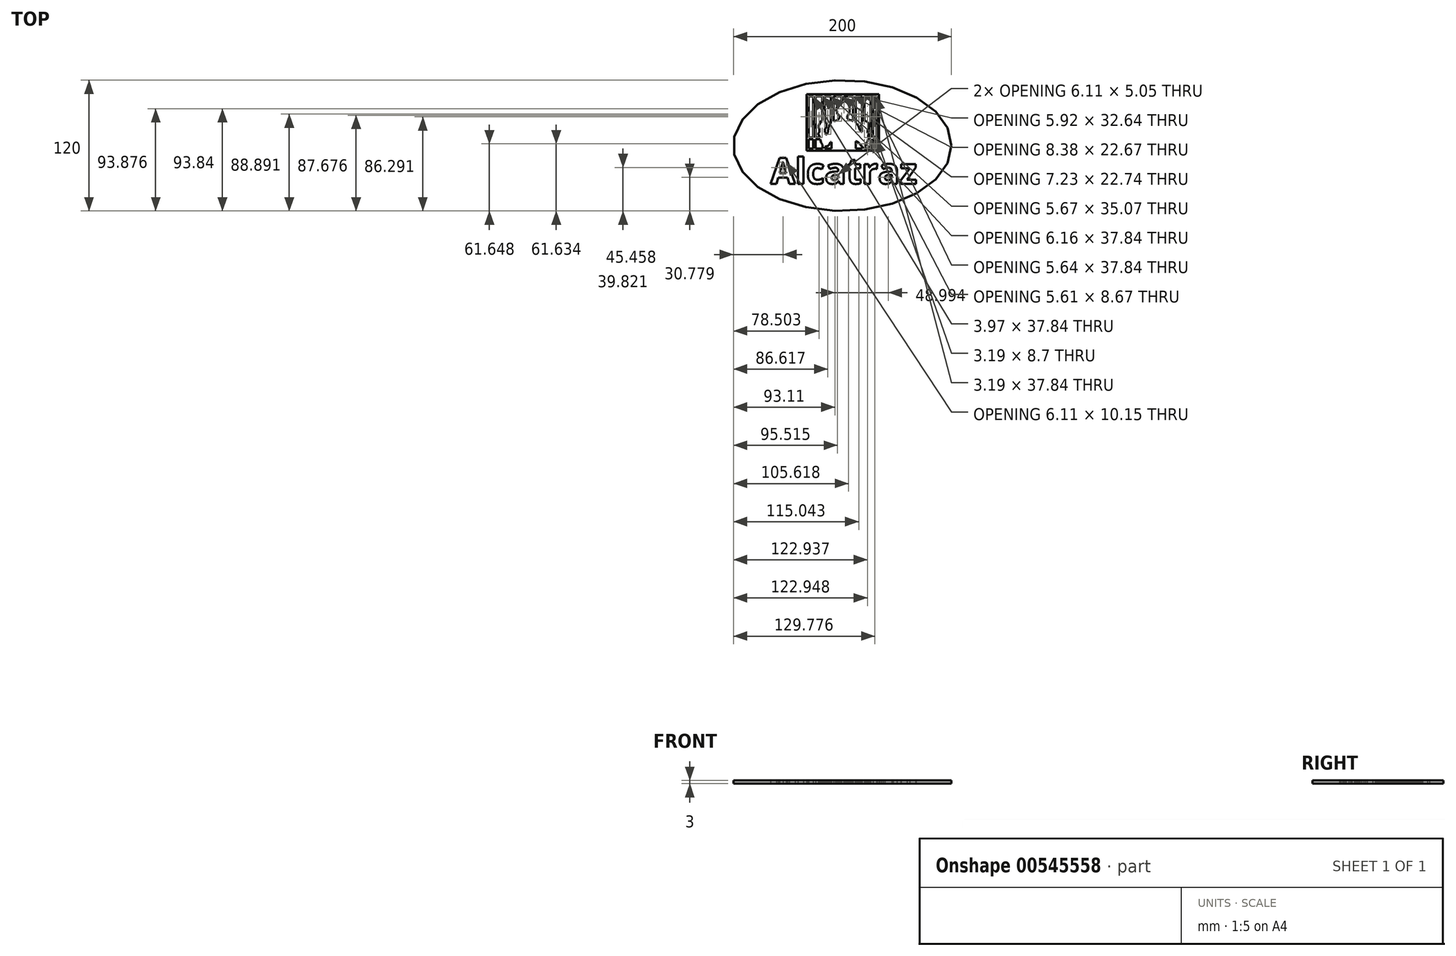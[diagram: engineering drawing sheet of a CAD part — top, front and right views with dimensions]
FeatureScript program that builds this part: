
annotation { "Feature Type Name" : "Feature", "Feature Type Description" : "" }
export const myFeature = defineFeature(function(context is Context, id is Id, definition is map)
    precondition{}
    {
        {
            var Q0;
            Q0=qCreatedBy(makeId("Top.planeOp"),FACE);
            var sketch = newSketch(context, id + "F0", { "sketchPlane" : qUnion([Q0])});
            skEllipse(sketch, "E0", {"center": v(0, 0) * mm, "majorRadius": 100 * mm, "minorRadius": 60 * mm, "majorAxis": v(1, 0)});
            skFitSpline(sketch, "E1.0", {"points": [v(94.93, -2.57) * mm, v(95.04, 0) * mm, v(94.93, 2.57) * mm, v(94.5, 5.97) * mm, v(93.46, 10.19) * mm, v(91.36, 15.2) * mm, v(88.41, 20.14) * mm, v(84.62, 24.96) * mm, v(80.76, 28.83) * mm, v(77.26, 31.82) * mm, v(74.43, 34) * mm, v(71.4, 36.11) * mm, v(68.17, 38.15) * mm, v(64.76, 40.1) * mm, v(61.2, 41.94) * mm, v(57.49, 43.68) * mm, v(52.36, 45.84) * mm, v(45.64, 48.25) * mm, v(37.12, 50.66) * mm, v(28.24, 52.57) * mm, v(20.58, 53.73) * mm, v(14.33, 54.39) * mm, v(9.6, 54.74) * mm, v(5.61, 54.92) * mm, v(2.4, 54.99) * mm, v(0, 55) * mm, v(-2.41, 54.99) * mm, v(-5.61, 54.92) * mm, v(-9.6, 54.74) * mm, v(-14.33, 54.39) * mm, v(-20.58, 53.73) * mm, v(-28.24, 52.57) * mm, v(-37.12, 50.66) * mm, v(-45.64, 48.25) * mm, v(-52.36, 45.84) * mm, v(-57.49, 43.68) * mm, v(-61.2, 41.94) * mm, v(-64.76, 40.1) * mm, v(-68.17, 38.15) * mm, v(-71.4, 36.11) * mm, v(-74.43, 34) * mm, v(-77.26, 31.82) * mm, v(-80.76, 28.83) * mm, v(-84.62, 24.96) * mm, v(-88.41, 20.14) * mm, v(-91.36, 15.2) * mm, v(-93.46, 10.19) * mm, v(-94.5, 5.97) * mm, v(-94.93, 2.57) * mm, v(-95.04, 0) * mm, v(-94.93, -2.57) * mm, v(-94.5, -5.97) * mm, v(-93.46, -10.19) * mm, v(-91.36, -15.2) * mm, v(-88.41, -20.14) * mm, v(-84.62, -24.96) * mm, v(-80.76, -28.83) * mm, v(-77.26, -31.82) * mm, v(-74.43, -34) * mm, v(-71.4, -36.11) * mm, v(-68.17, -38.15) * mm, v(-64.76, -40.1) * mm, v(-61.2, -41.94) * mm, v(-57.49, -43.68) * mm, v(-52.36, -45.84) * mm, v(-45.64, -48.25) * mm, v(-37.12, -50.66) * mm, v(-28.24, -52.57) * mm, v(-20.58, -53.73) * mm, v(-14.33, -54.39) * mm, v(-9.6, -54.74) * mm, v(-5.61, -54.92) * mm, v(-2.41, -54.99) * mm, v(0, -55) * mm, v(2.4, -54.99) * mm, v(5.61, -54.92) * mm, v(9.6, -54.74) * mm, v(14.33, -54.39) * mm, v(20.58, -53.73) * mm, v(28.24, -52.57) * mm, v(37.12, -50.66) * mm, v(45.64, -48.25) * mm, v(52.36, -45.84) * mm, v(57.49, -43.68) * mm, v(61.2, -41.94) * mm, v(64.76, -40.1) * mm, v(68.17, -38.15) * mm, v(71.4, -36.11) * mm, v(74.43, -34) * mm, v(77.26, -31.82) * mm, v(80.76, -28.83) * mm, v(84.62, -24.96) * mm, v(88.41, -20.14) * mm, v(91.36, -15.2) * mm, v(93.46, -10.19) * mm, v(94.5, -5.97) * mm, v(94.93, -2.57) * mm, v(95.04, 0) * mm, v(94.93, 2.57) * mm, v(94.93, -2.57) * mm]});
            skSolve(sketch);
        }
        {
            var Q0;
            Q0=makeQuery(id+"F0.imprint","IMPRINT",FACE,{"disambiguationData":[TD([[makeQuery(id+"F0.imprint","IMPRINT",EDGE,{"derivedFrom":sQuery(id+"F0.wireOp",EDGE,"E0")}),1.0]])]});
            var Q1;
            Q1=sQuery(id+"F0.wireOp",EDGE,"E0");
            var Q2;
            Q2=sQuery(id+"F0.wireOp",EDGE,"E1.0");
            extrude(context, id + "F1", {"entities" : qUnion([Q0]), "surfaceEntities" : qUnion([Q1, Q2]), "depth" : 3 * mm, "offsetDistance" : 25 * mm});
        }
        {
            var Q0;
            Q0=qCreatedBy(makeId("Top.planeOp"),FACE);
            var sketch = newSketch(context, id + "F2", { "sketchPlane" : qUnion([Q0])});
            skLineSegment(sketch, "E2", {"start": v(-10.03, -1.92) * mm, "end": v(-10.03, 2.73) * mm});
            skLineSegment(sketch, "E3", {"start": v(-10.03, 2.73) * mm, "end": v(-10.27, 3.12) * mm});
            skLineSegment(sketch, "E4", {"start": v(-10.27, 3.12) * mm, "end": v(-10.92, 3.12) * mm});
            skLineSegment(sketch, "E5", {"start": v(-10.92, 3.12) * mm, "end": v(-11.14, 2.54) * mm});
            skLineSegment(sketch, "E6", {"start": v(-11.14, 2.54) * mm, "end": v(-12.04, 0.97) * mm});
            skLineSegment(sketch, "E7", {"start": v(-12.04, 0.97) * mm, "end": v(-13.13, -0.16) * mm});
            skLineSegment(sketch, "E8", {"start": v(-13.13, -0.16) * mm, "end": v(-14.02, -0.56) * mm});
            skLineSegment(sketch, "E9", {"start": v(-14.02, -0.56) * mm, "end": v(-15.26, -0.93) * mm});
            skLineSegment(sketch, "E10", {"start": v(-15.26, -0.93) * mm, "end": v(-16.06, -1.25) * mm});
            skLineSegment(sketch, "E11", {"start": v(-16.06, -1.25) * mm, "end": v(-16.06, -2.7) * mm});
            skLineSegment(sketch, "E12", {"start": v(-18.4, -2.7) * mm, "end": v(-18.4, 0.7) * mm});
            skLineSegment(sketch, "E13", {"start": v(-18.4, 0.7) * mm, "end": v(-19.45, 2.73) * mm});
            skLineSegment(sketch, "E14", {"start": v(-19.45, 2.73) * mm, "end": v(-20.03, 4.87) * mm});
            skLineSegment(sketch, "E15", {"start": v(-20.03, 4.87) * mm, "end": v(-20.34, 5.95) * mm});
            skLineSegment(sketch, "E16", {"start": v(-20.9, 7.87) * mm, "end": v(-21.95, 10.53) * mm});
            skLineSegment(sketch, "E17", {"start": v(-21.95, 10.53) * mm, "end": v(-21.95, 11.44) * mm});
            skLineSegment(sketch, "E18", {"start": v(-21.95, 11.44) * mm, "end": v(-21.11, 12.31) * mm});
            skLineSegment(sketch, "E19", {"start": v(-21.11, 12.31) * mm, "end": v(-21.11, 14.95) * mm});
            skLineSegment(sketch, "E20", {"start": v(-21.11, 14.95) * mm, "end": v(-21.47, 15.85) * mm});
            skLineSegment(sketch, "E21", {"start": v(-21.47, 15.85) * mm, "end": v(-21.74, 16.52) * mm});
            skLineSegment(sketch, "E22", {"start": v(-21.74, 16.52) * mm, "end": v(-21.74, 18.05) * mm});
            skLineSegment(sketch, "E23", {"start": v(-21.74, 18.05) * mm, "end": v(-21.02, 19.76) * mm});
            skLineSegment(sketch, "E24", {"start": v(-21.02, 19.76) * mm, "end": v(-20.4, 20.86) * mm});
            skLineSegment(sketch, "E25", {"start": v(-20.4, 20.86) * mm, "end": v(-19.66, 22.15) * mm});
            skLineSegment(sketch, "E26", {"start": v(-19.66, 22.15) * mm, "end": v(-18.79, 23.06) * mm});
            skLineSegment(sketch, "E27", {"start": v(-18.79, 23.06) * mm, "end": v(-18.42, 23.71) * mm});
            skLineSegment(sketch, "E28", {"start": v(-16.02, 21.41) * mm, "end": v(-14.77, 20.7) * mm});
            skLineSegment(sketch, "E29", {"start": v(-14.77, 20.7) * mm, "end": v(-14.55, 19.32) * mm});
            skLineSegment(sketch, "E30", {"start": v(-14.55, 19.32) * mm, "end": v(-14.55, 18.27) * mm});
            skLineSegment(sketch, "E31", {"start": v(-14.55, 18.27) * mm, "end": v(-14.55, 17.44) * mm});
            skLineSegment(sketch, "E32", {"start": v(-14.55, 17.44) * mm, "end": v(-14.55, 16.77) * mm});
            skLineSegment(sketch, "E33", {"start": v(-14.55, 16.77) * mm, "end": v(-15.6, 15.69) * mm});
            skLineSegment(sketch, "E34", {"start": v(-15.6, 15.69) * mm, "end": v(-16.07, 14.86) * mm});
            skLineSegment(sketch, "E35", {"start": v(-16.07, 14.86) * mm, "end": v(-16.07, 12.9) * mm});
            skLineSegment(sketch, "E36", {"start": v(-16.07, 12.9) * mm, "end": v(-15.7, 11.97) * mm});
            skLineSegment(sketch, "E37", {"start": v(-15.7, 11.97) * mm, "end": v(-15.26, 10.85) * mm});
            skLineSegment(sketch, "E38", {"start": v(-15.26, 10.85) * mm, "end": v(-15.26, 10.14) * mm});
            skLineSegment(sketch, "E39", {"start": v(-15.26, 10.14) * mm, "end": v(-14.5, 10.14) * mm});
            skLineSegment(sketch, "E40", {"start": v(-14.5, 10.14) * mm, "end": v(-13.85, 11.27) * mm});
            skLineSegment(sketch, "E41", {"start": v(-13.85, 11.27) * mm, "end": v(-13.27, 12.3) * mm});
            skLineSegment(sketch, "E42", {"start": v(-13.27, 12.3) * mm, "end": v(-13.13, 13.73) * mm});
            skLineSegment(sketch, "E43", {"start": v(-13.13, 13.73) * mm, "end": v(-12.8, 15.35) * mm});
            skLineSegment(sketch, "E44", {"start": v(-12.8, 15.35) * mm, "end": v(-12.46, 17.15) * mm});
            skLineSegment(sketch, "E45", {"start": v(-12.46, 17.15) * mm, "end": v(-11.9, 18.58) * mm});
            skLineSegment(sketch, "E46", {"start": v(-11.9, 18.58) * mm, "end": v(-11.2, 19.79) * mm});
            skLineSegment(sketch, "E47", {"start": v(-11.2, 19.79) * mm, "end": v(-10.55, 20.93) * mm});
            skLineSegment(sketch, "E48", {"start": v(-10.55, 20.93) * mm, "end": v(-10.55, 20.93) * mm});
            skLineSegment(sketch, "E49", {"start": v(-8.1, 22.47) * mm, "end": v(-6.35, 22.74) * mm});
            skLineSegment(sketch, "E50", {"start": v(-6.35, 22.74) * mm, "end": v(-4.99, 23.28) * mm});
            skLineSegment(sketch, "E51", {"start": v(-4.99, 23.28) * mm, "end": v(-3.74, 24.22) * mm});
            skLineSegment(sketch, "E52", {"start": v(-3.74, 24.22) * mm, "end": v(-2.88, 25.11) * mm});
            skLineSegment(sketch, "E53", {"start": v(-2.88, 25.11) * mm, "end": v(-2.3, 26.15) * mm});
            skLineSegment(sketch, "E54", {"start": v(-2.3, 26.15) * mm, "end": v(-2.5, 26.7) * mm});
            skLineSegment(sketch, "E55", {"start": v(-2.5, 26.7) * mm, "end": v(-3.29, 27.44) * mm});
            skLineSegment(sketch, "E56", {"start": v(-3.29, 27.44) * mm, "end": v(-4.06, 28.18) * mm});
            skLineSegment(sketch, "E57", {"start": v(-4.06, 28.18) * mm, "end": v(-4.55, 29.11) * mm});
            skLineSegment(sketch, "E58", {"start": v(-4.55, 29.11) * mm, "end": v(-4.92, 30.06) * mm});
            skLineSegment(sketch, "E59", {"start": v(-4.92, 30.06) * mm, "end": v(-4.92, 31.2) * mm});
            skLineSegment(sketch, "E60", {"start": v(-4.92, 31.2) * mm, "end": v(-5.13, 32.19) * mm});
            skLineSegment(sketch, "E61", {"start": v(-5.13, 32.19) * mm, "end": v(-5.13, 33.32) * mm});
            skLineSegment(sketch, "E62", {"start": v(-5.13, 33.32) * mm, "end": v(-5.13, 34.72) * mm});
            skLineSegment(sketch, "E63", {"start": v(-5.13, 34.72) * mm, "end": v(-4.99, 35.74) * mm});
            skLineSegment(sketch, "E64", {"start": v(-4.99, 35.74) * mm, "end": v(-4.57, 36.85) * mm});
            skLineSegment(sketch, "E65", {"start": v(-4.57, 36.85) * mm, "end": v(-3.92, 37.99) * mm});
            skLineSegment(sketch, "E66", {"start": v(-3.92, 37.99) * mm, "end": v(-3.16, 39.05) * mm});
            skLineSegment(sketch, "E67", {"start": v(-3.16, 39.05) * mm, "end": v(-2.07, 40.2) * mm});
            skLineSegment(sketch, "E68", {"start": v(-2.07, 40.2) * mm, "end": v(-0.87, 40.91) * mm});
            skLineSegment(sketch, "E69", {"start": v(1.43, 40.91) * mm, "end": v(2.56, 40.48) * mm});
            skLineSegment(sketch, "E70", {"start": v(2.56, 40.48) * mm, "end": v(3.54, 39.92) * mm});
            skLineSegment(sketch, "E71", {"start": v(3.54, 39.92) * mm, "end": v(4.3, 39.2) * mm});
            skLineSegment(sketch, "E72", {"start": v(4.3, 39.2) * mm, "end": v(5.12, 38.11) * mm});
            skLineSegment(sketch, "E73", {"start": v(5.12, 38.11) * mm, "end": v(5.78, 36.9) * mm});
            skLineSegment(sketch, "E74", {"start": v(5.78, 36.9) * mm, "end": v(6.25, 35.7) * mm});
            skLineSegment(sketch, "E75", {"start": v(6.25, 35.7) * mm, "end": v(6.54, 34.56) * mm});
            skLineSegment(sketch, "E76", {"start": v(6.54, 34.56) * mm, "end": v(6.62, 33.24) * mm});
            skLineSegment(sketch, "E77", {"start": v(6.62, 33.24) * mm, "end": v(6.62, 31.45) * mm});
            skLineSegment(sketch, "E78", {"start": v(6.62, 31.45) * mm, "end": v(6.44, 30.1) * mm});
            skLineSegment(sketch, "E79", {"start": v(6.44, 30.1) * mm, "end": v(5.72, 28.86) * mm});
            skLineSegment(sketch, "E80", {"start": v(5.72, 28.86) * mm, "end": v(5.05, 27.68) * mm});
            skLineSegment(sketch, "E81", {"start": v(5.05, 27.68) * mm, "end": v(4.71, 26.8) * mm});
            skLineSegment(sketch, "E82", {"start": v(4.71, 26.8) * mm, "end": v(4.43, 26.04) * mm});
            skLineSegment(sketch, "E83", {"start": v(4.43, 26.04) * mm, "end": v(4.48, 25.26) * mm});
            skLineSegment(sketch, "E84", {"start": v(4.48, 25.26) * mm, "end": v(4.76, 24.55) * mm});
            skLineSegment(sketch, "E85", {"start": v(4.76, 24.55) * mm, "end": v(5.54, 24.1) * mm});
            skLineSegment(sketch, "E86", {"start": v(5.54, 24.1) * mm, "end": v(6.25, 23.56) * mm});
            skLineSegment(sketch, "E87", {"start": v(6.25, 23.56) * mm, "end": v(7.38, 23.28) * mm});
            skLineSegment(sketch, "E88", {"start": v(7.38, 23.28) * mm, "end": v(8.42, 23) * mm});
            skLineSegment(sketch, "E89", {"start": v(8.42, 23) * mm, "end": v(9.28, 22.68) * mm});
            skLineSegment(sketch, "E90", {"start": v(9.28, 22.68) * mm, "end": v(9.81, 22.54) * mm});
            skLineSegment(sketch, "E91", {"start": v(12.08, 20.89) * mm, "end": v(13.03, 19.98) * mm});
            skLineSegment(sketch, "E92", {"start": v(13.03, 19.98) * mm, "end": v(13.9, 19.26) * mm});
            skLineSegment(sketch, "E93", {"start": v(13.9, 19.26) * mm, "end": v(14.45, 18.55) * mm});
            skLineSegment(sketch, "E94", {"start": v(14.45, 18.55) * mm, "end": v(14.7, 17.9) * mm});
            skLineSegment(sketch, "E95", {"start": v(14.7, 17.9) * mm, "end": v(14.92, 17.34) * mm});
            skLineSegment(sketch, "E96", {"start": v(14.92, 17.34) * mm, "end": v(15.2, 16.65) * mm});
            skLineSegment(sketch, "E97", {"start": v(15.2, 16.65) * mm, "end": v(15.5, 15.9) * mm});
            skLineSegment(sketch, "E98", {"start": v(15.5, 15.9) * mm, "end": v(15.78, 15.17) * mm});
            skLineSegment(sketch, "E99", {"start": v(15.78, 15.17) * mm, "end": v(16.04, 14.51) * mm});
            skLineSegment(sketch, "E100", {"start": v(16.04, 14.51) * mm, "end": v(16.09, 13.77) * mm});
            skLineSegment(sketch, "E101", {"start": v(16.09, 13.77) * mm, "end": v(16.75, 13.29) * mm});
            skLineSegment(sketch, "E102", {"start": v(16.75, 13.29) * mm, "end": v(17.25, 12.81) * mm});
            skLineSegment(sketch, "E103", {"start": v(17.25, 12.81) * mm, "end": v(17.67, 12.57) * mm});
            skLineSegment(sketch, "E104", {"start": v(17.67, 12.57) * mm, "end": v(18, 12.57) * mm});
            skLineSegment(sketch, "E105", {"start": v(18, 12.57) * mm, "end": v(18, 16.92) * mm});
            skLineSegment(sketch, "E106", {"start": v(18, 16.92) * mm, "end": v(17.53, 17.38) * mm});
            skLineSegment(sketch, "E107", {"start": v(17.53, 17.38) * mm, "end": v(17.14, 17.9) * mm});
            skLineSegment(sketch, "E108", {"start": v(17.14, 17.9) * mm, "end": v(16.9, 18.2) * mm});
            skLineSegment(sketch, "E109", {"start": v(16.9, 18.2) * mm, "end": v(16.87, 18.78) * mm});
            skLineSegment(sketch, "E110", {"start": v(16.87, 18.78) * mm, "end": v(17.5, 19.44) * mm});
            skLineSegment(sketch, "E111", {"start": v(17.5, 19.44) * mm, "end": v(17.9, 19.85) * mm});
            skLineSegment(sketch, "E112", {"start": v(17.9, 19.85) * mm, "end": v(17.9, 45.21) * mm});
            skLineSegment(sketch, "E113", {"start": v(20.12, 45.21) * mm, "end": v(20.12, 22.29) * mm});
            skLineSegment(sketch, "E114", {"start": v(20.12, 22.29) * mm, "end": v(21, 22.63) * mm});
            skLineSegment(sketch, "E115", {"start": v(21, 22.63) * mm, "end": v(21.51, 22.56) * mm});
            skLineSegment(sketch, "E116", {"start": v(21.51, 22.56) * mm, "end": v(22.25, 22.14) * mm});
            skLineSegment(sketch, "E117", {"start": v(22.25, 22.14) * mm, "end": v(23.2, 20.89) * mm});
            skLineSegment(sketch, "E118", {"start": v(23.2, 20.89) * mm, "end": v(24, 20.43) * mm});
            skLineSegment(sketch, "E119", {"start": v(24, 20.43) * mm, "end": v(24.46, 19.26) * mm});
            skLineSegment(sketch, "E120", {"start": v(24.46, 19.26) * mm, "end": v(24.46, 17.38) * mm});
            skLineSegment(sketch, "E121", {"start": v(24.46, 17.38) * mm, "end": v(24.55, 15.9) * mm});
            skLineSegment(sketch, "E122", {"start": v(24.55, 15.9) * mm, "end": v(23.62, 14.94) * mm});
            skLineSegment(sketch, "E123", {"start": v(23.62, 14.94) * mm, "end": v(23.03, 13.9) * mm});
            skLineSegment(sketch, "E124", {"start": v(23.03, 13.9) * mm, "end": v(22.94, 13.67) * mm});
            skLineSegment(sketch, "E125", {"start": v(22.94, 13.67) * mm, "end": v(23.07, 11.57) * mm});
            skLineSegment(sketch, "E126", {"start": v(23.07, 11.57) * mm, "end": v(23.48, 11.47) * mm});
            skLineSegment(sketch, "E127", {"start": v(23.48, 11.47) * mm, "end": v(23.98, 11.28) * mm});
            skLineSegment(sketch, "E128", {"start": v(23.98, 11.28) * mm, "end": v(24.18, 11.17) * mm});
            skLineSegment(sketch, "E129", {"start": v(24.18, 11.17) * mm, "end": v(23.97, 10.7) * mm});
            skLineSegment(sketch, "E130", {"start": v(23.97, 10.7) * mm, "end": v(23.84, 10) * mm});
            skLineSegment(sketch, "E131", {"start": v(23.84, 10) * mm, "end": v(23.7, 8.92) * mm});
            skLineSegment(sketch, "E132", {"start": v(23.7, 8.92) * mm, "end": v(23.7, 8) * mm});
            skLineSegment(sketch, "E133", {"start": v(23.7, 8) * mm, "end": v(23.57, 7.37) * mm});
            skLineSegment(sketch, "E134", {"start": v(23.28, 5.95) * mm, "end": v(23.05, 4.73) * mm});
            skLineSegment(sketch, "E135", {"start": v(23.05, 4.73) * mm, "end": v(22.9, 4) * mm});
            skLineSegment(sketch, "E136", {"start": v(22.9, 4) * mm, "end": v(22.62, 3.23) * mm});
            skLineSegment(sketch, "E137", {"start": v(22.62, 3.23) * mm, "end": v(22.1, 1.87) * mm});
            skLineSegment(sketch, "E138", {"start": v(22.1, 1.87) * mm, "end": v(21.69, 0.78) * mm});
            skLineSegment(sketch, "E139", {"start": v(21.69, 0.78) * mm, "end": v(21.25, -0.38) * mm});
            skLineSegment(sketch, "E140", {"start": v(21.25, -0.38) * mm, "end": v(20.94, -0.93) * mm});
            skLineSegment(sketch, "E141", {"start": v(20.94, -0.93) * mm, "end": v(20.73, -1.29) * mm});
            skLineSegment(sketch, "E142", {"start": v(20.73, -1.29) * mm, "end": v(20.14, -1.29) * mm});
            skLineSegment(sketch, "E143", {"start": v(18.02, -0.27) * mm, "end": v(17.13, 0.24) * mm});
            skLineSegment(sketch, "E144", {"start": v(17.13, 0.24) * mm, "end": v(16.33, 1.03) * mm});
            skLineSegment(sketch, "E145", {"start": v(16.33, 1.03) * mm, "end": v(15.5, 1.83) * mm});
            skLineSegment(sketch, "E146", {"start": v(15.5, 1.83) * mm, "end": v(14.76, 2.53) * mm});
            skLineSegment(sketch, "E147", {"start": v(14.76, 2.53) * mm, "end": v(13.9, 3.15) * mm});
            skLineSegment(sketch, "E148", {"start": v(13.9, 3.15) * mm, "end": v(13.13, 3.72) * mm});
            skLineSegment(sketch, "E149", {"start": v(13.13, 3.72) * mm, "end": v(12.58, 4.03) * mm});
            skLineSegment(sketch, "E150", {"start": v(12.58, 4.03) * mm, "end": v(12.3, 3.92) * mm});
            skLineSegment(sketch, "E151", {"start": v(12.3, 3.92) * mm, "end": v(12.3, 3.02) * mm});
            skLineSegment(sketch, "E152", {"start": v(12.3, 3.02) * mm, "end": v(12.37, 1.88) * mm});
            skLineSegment(sketch, "E153", {"start": v(12.37, 1.88) * mm, "end": v(12.37, 0.66) * mm});
            skLineSegment(sketch, "E154", {"start": v(12.37, 0.66) * mm, "end": v(12.37, -1.92) * mm});
            skLineSegment(sketch, "E155", {"start": v(25.76, 45.21) * mm, "end": v(25.76, 7.37) * mm});
            skLineSegment(sketch, "E156", {"start": v(28.18, -2.7) * mm, "end": v(28.18, 5.98) * mm});
            skLineSegment(sketch, "E157", {"start": v(12.08, 45.21) * mm, "end": v(12.08, 20.89) * mm});
            skLineSegment(sketch, "E158", {"start": v(9.81, 45.21) * mm, "end": v(9.81, 22.54) * mm});
            skLineSegment(sketch, "E159", {"start": v(12.37, -1.92) * mm, "end": v(12.37, -2.7) * mm});
            skLineSegment(sketch, "E160", {"start": v(-10.03, -2.7) * mm, "end": v(-10.03, -1.92) * mm});
            skLineSegment(sketch, "E161", {"start": v(18.02, -0.27) * mm, "end": v(18.02, -2.7) * mm});
            skLineSegment(sketch, "E162", {"start": v(20.14, -2.7) * mm, "end": v(20.14, -1.29) * mm});
            skLineSegment(sketch, "E163", {"start": v(31.37, 6) * mm, "end": v(28.18, 5.98) * mm});
            skLineSegment(sketch, "E164", {"start": v(31.36, 7.37) * mm, "end": v(28.18, 7.37) * mm});
            skLineSegment(sketch, "E165.trimOffspring", {"start": v(25.76, 5.97) * mm, "end": v(25.76, -2.7) * mm});
            skLineSegment(sketch, "E166.trimOffspring", {"start": v(28.18, 7.37) * mm, "end": v(28.18, 45.21) * mm});
            skLineSegment(sketch, "E167.trimOffspring", {"start": v(25.76, 5.97) * mm, "end": v(23.28, 5.95) * mm});
            skLineSegment(sketch, "E168.trimOffspring", {"start": v(25.76, 7.37) * mm, "end": v(23.57, 7.37) * mm});
            skLineSegment(sketch, "E169", {"start": v(-24.58, -2.7) * mm, "end": v(-24.58, 5.95) * mm});
            skLineSegment(sketch, "E170", {"start": v(-26.85, 45.21) * mm, "end": v(-26.85, 7.37) * mm});
            skLineSegment(sketch, "E171", {"start": v(23.28, 5.95) * mm, "end": v(-24.58, 5.95) * mm});
            skLineSegment(sketch, "E172", {"start": v(23.57, 7.37) * mm, "end": v(-24.58, 7.37) * mm});
            skPoint(sketch, "E172.endSnap0", {"position": v(24.66, 7.37) * mm});
            skLineSegment(sketch, "E173.trimOffspring", {"start": v(-26.85, 5.95) * mm, "end": v(-26.85, -2.7) * mm});
            skLineSegment(sketch, "E174.trimOffspring", {"start": v(-24.58, 7.37) * mm, "end": v(-24.58, 45.21) * mm});
            skLineSegment(sketch, "E175.trimOffspring", {"start": v(-26.85, 7.37) * mm, "end": v(-30.82, 7.37) * mm});
            skLineSegment(sketch, "E176.trimOffspring", {"start": v(-26.85, 5.95) * mm, "end": v(-30.82, 5.95) * mm});
            skLineSegment(sketch, "E177.trimOffspring", {"start": v(-20.75, 7.37) * mm, "end": v(-20.9, 7.87) * mm});
            skLineSegment(sketch, "E178", {"start": v(-18.42, 45.21) * mm, "end": v(-18.42, 23.71) * mm});
            skLineSegment(sketch, "E179", {"start": v(-16.22, 45.21) * mm, "end": v(-16.02, 21.41) * mm});
            skLineSegment(sketch, "E180", {"start": v(-8.1, 45.21) * mm, "end": v(-8.1, 22.47) * mm});
            skLineSegment(sketch, "E181", {"start": v(-10.55, 45.21) * mm, "end": v(-10.55, 20.93) * mm});
            skLineSegment(sketch, "E182", {"start": v(-0.87, 45.21) * mm, "end": v(-0.87, 40.91) * mm});
            skLineSegment(sketch, "E183", {"start": v(1.43, 45.21) * mm, "end": v(1.43, 40.91) * mm});
            skLineSegment(sketch, "E184", {"start": v(31.37, -2.7) * mm, "end": v(31.37, 6) * mm});
            skLineSegment(sketch, "E185", {"start": v(-30.82, 45.21) * mm, "end": v(-30.82, -2.7) * mm});
            skLineSegment(sketch, "E186", {"start": v(31.37, 45.21) * mm, "end": v(-30.82, 45.21) * mm});
            skLineSegment(sketch, "E187", {"start": v(-30.82, -2.7) * mm, "end": v(25.76, -2.7) * mm});
            skLineSegment(sketch, "E188.0", {"start": v(33.37, 47.21) * mm, "end": v(-32.82, 47.21) * mm});
            skLineSegment(sketch, "E188.1", {"start": v(33.37, -4.7) * mm, "end": v(33.37, 47.21) * mm});
            skLineSegment(sketch, "E188.2", {"start": v(-32.82, -4.7) * mm, "end": v(33.37, -4.7) * mm});
            skLineSegment(sketch, "E188.3", {"start": v(-32.82, 47.21) * mm, "end": v(-32.82, -4.7) * mm});
            skLineSegment(sketch, "E189.trimOffspring", {"start": v(28.18, -2.7) * mm, "end": v(31.37, -2.7) * mm});
            skLineSegment(sketch, "E190", {"start": v(31.36, 7.37) * mm, "end": v(31.37, 45.21) * mm});
            skSolve(sketch);
        }
        {
            var Q0;
            Q0=qCreatedBy(makeId("Top.planeOp"),FACE);
            var sketch = newSketch(context, id + "F3", { "sketchPlane" : qUnion([Q0])});
            skText(sketch, "E191", { "text": "Alcatraz", "fontName": "OpenSans-Bold.ttf"});
            const initialGuessF3  = {"E191": [-0.0659, -0.035, 1, 0, 0.02364]};
            skSetInitialGuess(sketch, initialGuessF3);
            skSolve(sketch);
        }
        {
            var Q0;
            Q0=makeQuery(id+"F2.imprint","IMPRINT",FACE,{"disambiguationData":[TD([[makeQuery(id+"F2.imprint","IMPRINT",EDGE,{"derivedFrom":sQuery(id+"F2.wireOp",EDGE,"E16")}),-1.0]])]});
            var Q1;
            Q1=makeQuery(id+"F2.imprint","IMPRINT",FACE,{"disambiguationData":[TD([[makeQuery(id+"F2.imprint","IMPRINT",EDGE,{"derivedFrom":sQuery(id+"F2.wireOp",EDGE,"E2")}),-1.0]])]});
            var Q2;
            Q2=makeQuery(id+"F2.imprint","IMPRINT",FACE,{"disambiguationData":[TD([[makeQuery(id+"F2.imprint","IMPRINT",EDGE,{"derivedFrom":sQuery(id+"F2.wireOp",EDGE,"E188.0")}),1.0]])]});
            extrude(context, id + "F4", {"entities" : qUnion([Q0, Q1, Q2]), "depth" : 3 * mm, "offsetDistance" : 25 * mm});
        }
        {
            var Q0;
            Q0=makeQuery(id+"F3.imprint","IMPRINT",FACE,{"disambiguationData":[TD([[makeQuery(id+"F3.imprint","IMPRINT",EDGE,{"derivedFrom":sQuery(id+"F3.wireOp",EDGE,"E191.sketch_text.stroke-0")}),-1.0]])]});
            var Q1;
            Q1=makeQuery(id+"F3.imprint","IMPRINT",FACE,{"disambiguationData":[TD([[makeQuery(id+"F3.imprint","IMPRINT",EDGE,{"derivedFrom":sQuery(id+"F3.wireOp",EDGE,"E191.sketch_text.stroke-16")}),-1.0]])]});
            var Q2;
            Q2=makeQuery(id+"F3.imprint","IMPRINT",FACE,{"disambiguationData":[TD([[makeQuery(id+"F3.imprint","IMPRINT",EDGE,{"derivedFrom":sQuery(id+"F3.wireOp",EDGE,"E191.sketch_text.stroke-30")}),-1.0]])]});
            var Q3;
            Q3=makeQuery(id+"F3.imprint","IMPRINT",FACE,{"disambiguationData":[TD([[makeQuery(id+"F3.imprint","IMPRINT",EDGE,{"derivedFrom":sQuery(id+"F3.wireOp",EDGE,"E191.sketch_text.stroke-111")}),-1.0]])]});
            var Q4;
            Q4=makeQuery(id+"F3.imprint","IMPRINT",FACE,{"disambiguationData":[TD([[makeQuery(id+"F3.imprint","IMPRINT",EDGE,{"derivedFrom":sQuery(id+"F3.wireOp",EDGE,"E191.sketch_text.stroke-73")}),-1.0]])]});
            var Q5;
            Q5=makeQuery(id+"F3.imprint","IMPRINT",FACE,{"disambiguationData":[TD([[makeQuery(id+"F3.imprint","IMPRINT",EDGE,{"derivedFrom":sQuery(id+"F3.wireOp",EDGE,"E191.sketch_text.stroke-55")}),-1.0]])]});
            var Q6;
            Q6=makeQuery(id+"F3.imprint","IMPRINT",FACE,{"disambiguationData":[TD([[makeQuery(id+"F3.imprint","IMPRINT",EDGE,{"derivedFrom":sQuery(id+"F3.wireOp",EDGE,"E191.sketch_text.stroke-86")}),-1.0]])]});
            var Q7;
            Q7=makeQuery(id+"F3.imprint","IMPRINT",FACE,{"disambiguationData":[TD([[makeQuery(id+"F3.imprint","IMPRINT",EDGE,{"derivedFrom":sQuery(id+"F3.wireOp",EDGE,"E191.sketch_text.stroke-12")}),-1.0]])]});
            extrude(context, id + "F5", {"entities" : qUnion([Q0, Q1, Q2, Q3, Q4, Q5, Q6, Q7]), "depth" : 3 * mm, "offsetDistance" : 25 * mm});
        }
    });
